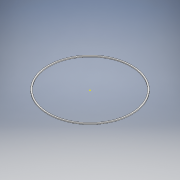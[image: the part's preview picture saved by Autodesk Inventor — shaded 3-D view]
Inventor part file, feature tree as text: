
AUTODESK INVENTOR PART (.ipt)
format: ipt  version: 2022 (Build 260153000, 153)  size: 124,416 bytes
history: native  units: mm
features: sketch x4, extrude x3
ambient origin geometry x8: Origin, YZ Plane, XZ Plane, XY Plane, X Axis, Y Axis, Z Axis, Center Point
bodies: Solid1 (feature_tree)
feature tree (7):
  extrude  "Extrusion1"  Depth=50.0mm TaperAngle=0.0deg
  sketch  "Sketch2"  dims[d6=20.0mm d7=0.0mm d8=0.0mm d9=0.0mm]
  extrude  "Extrusion2"  TaperAngle=0.0deg  [1 undecoded]
  extrude  "Extrusion3"  [1 undecoded]
  sketch  "Sketch1"  dims[d0=5050.0mm d4=50.0mm d5=0.0mm]
  sketch  "Sketch3"
  sketch  "Sketch4"
note: 2 required parameter values undecoded (feature->parameter linkage not recoverable at this tier; creation-order binding heuristic only, values carry confidence <= 0.55)
